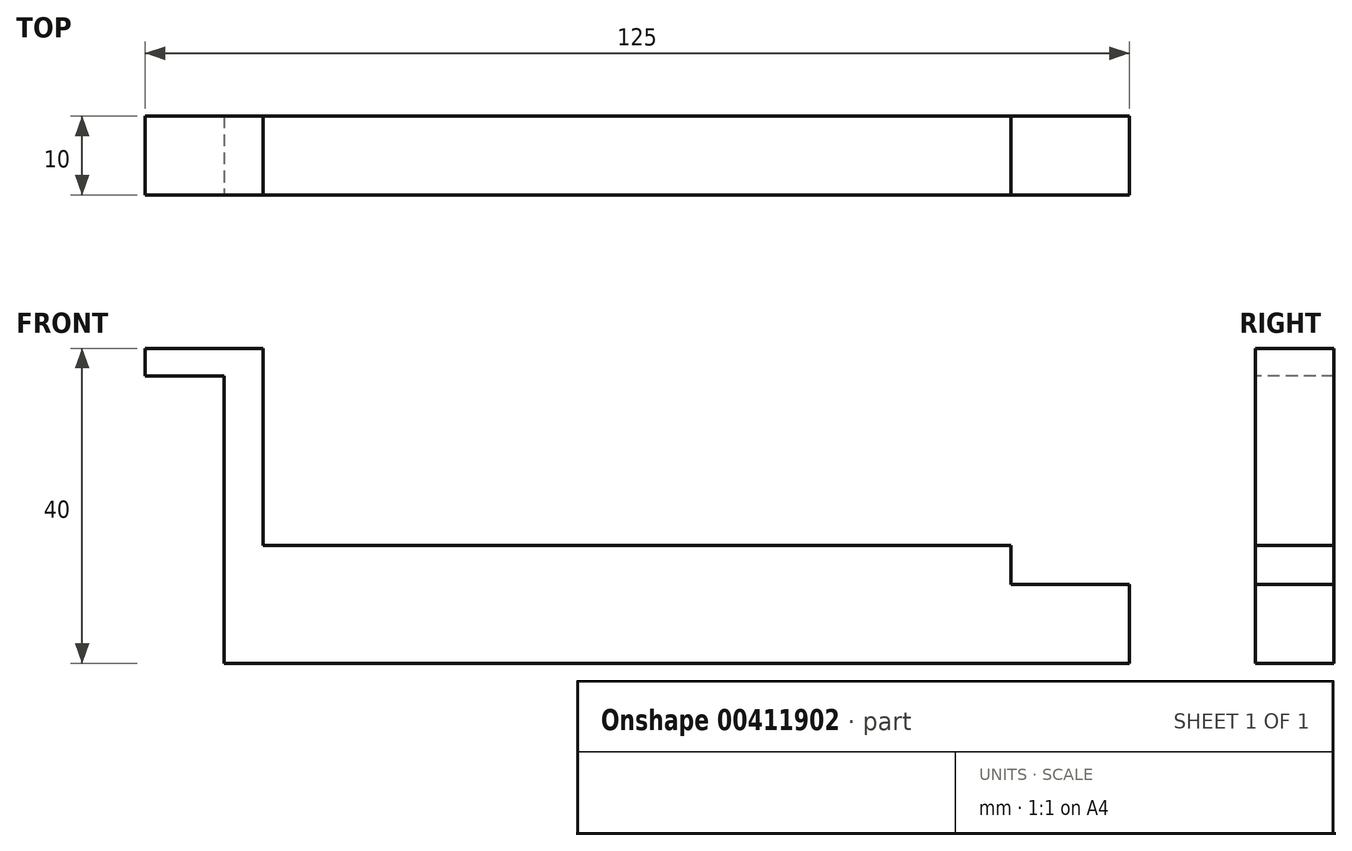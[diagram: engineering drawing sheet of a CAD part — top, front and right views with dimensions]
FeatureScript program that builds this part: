
annotation { "Feature Type Name" : "Feature", "Feature Type Description" : "" }
export const myFeature = defineFeature(function(context is Context, id is Id, definition is map)
    precondition{}
    {
        {
            var Q0;
            Q0=qCreatedBy(makeId("Front.planeOp"),FACE);
            var sketch = newSketch(context, id + "F0", { "sketchPlane" : qUnion([Q0])});
            skLineSegment(sketch, "E0.bottom", {"start": v(-57.5, 7.5) * mm, "end": v(57.5, 7.5) * mm});
            skLineSegment(sketch, "E0.top", {"start": v(-57.5, -7.5) * mm, "end": v(57.5, -7.5) * mm});
            skLineSegment(sketch, "E0.left", {"start": v(-57.5, 7.5) * mm, "end": v(-57.5, -7.5) * mm});
            skLineSegment(sketch, "E0.right", {"start": v(57.5, 7.5) * mm, "end": v(57.5, -7.5) * mm});
            skSolve(sketch);
        }
        {
            var Q0;
            Q0 = qSketchRegion(id + "F0", true);
            extrude(context, id + "F1", {"entities" : qUnion([Q0]), "depth" : 10 * mm});
        }
        {
            var Q0;
            Q0=makeQuery(id+"F1.opExtrude","SWEPT_FACE",FACE,{"disambiguationData":[OSD([sQuery(id+"F0.wireOp",EDGE,"E0.bottom")])]});
            var sketch = newSketch(context, id + "F2", { "sketchPlane" : qUnion([Q0])});
            skLineSegment(sketch, "E1.bottom", {"start": v(57.5, 0) * mm, "end": v(42.5, 0) * mm});
            skLineSegment(sketch, "E1.top", {"start": v(57.5, -10) * mm, "end": v(42.5, -10) * mm});
            skLineSegment(sketch, "E1.left", {"start": v(57.5, 0) * mm, "end": v(57.5, -10) * mm});
            skLineSegment(sketch, "E1.right", {"start": v(42.5, 0) * mm, "end": v(42.5, -10) * mm});
            skSolve(sketch);
        }
        {
            var Q0;
            Q0=makeQuery(id+"F2.imprint","IMPRINT",FACE,{"disambiguationData":[TD([[makeQuery(id+"F2.imprint","IMPRINT",EDGE,{"derivedFrom":sQuery(id+"F2.wireOp",EDGE,"E1.bottom")}),-1.0]])]});
            extrude(context, id + "F3", {"entities" : qUnion([Q0]), "operationType" : NewBodyOperationType.REMOVE, "oppositeDirection" : true, "depth" : 5 * mm});
        }
        {
            var Q0;
            Q0=makeQuery(id+"F1.opExtrude","SWEPT_FACE",FACE,{"disambiguationData":[OSD([sQuery(id+"F0.wireOp",EDGE,"E0.bottom")])]});
            var sketch = newSketch(context, id + "F4", { "sketchPlane" : qUnion([Q0])});
            skLineSegment(sketch, "E2.bottom", {"start": v(-52.5, 0) * mm, "end": v(-57.5, 0) * mm});
            skLineSegment(sketch, "E2.top", {"start": v(-52.5, -10) * mm, "end": v(-57.5, -10) * mm});
            skLineSegment(sketch, "E2.left", {"start": v(-52.5, 0) * mm, "end": v(-52.5, -10) * mm});
            skLineSegment(sketch, "E2.right", {"start": v(-57.5, 0) * mm, "end": v(-57.5, -10) * mm});
            skSolve(sketch);
        }
        {
            var Q0;
            Q0=makeQuery(id+"F4.imprint","IMPRINT",FACE,{"disambiguationData":[TD([[makeQuery(id+"F4.imprint","IMPRINT",EDGE,{"derivedFrom":sQuery(id+"F4.wireOp",EDGE,"E2.bottom")}),-1.0]])]});
            extrude(context, id + "F5", {"entities" : qUnion([Q0]), "operationType" : NewBodyOperationType.ADD, "depth" : 25 * mm});
        }
        {
            var Q0;
            Q0=makeQuery(id+"F5.boolean.opBoolean","MERGE",FACE,{"derivedFrom":[makeQuery(id+"F1.opExtrude","SWEPT_FACE",FACE,{"disambiguationData":[OSD([sQuery(id+"F0.wireOp",EDGE,"E0.left")])]}),makeQuery(id+"F5.opExtrude","SWEPT_FACE",FACE,{"disambiguationData":[OSD([sQuery(id+"F4.wireOp",EDGE,"E2.right")])]})]});
            var sketch = newSketch(context, id + "F6", { "sketchPlane" : qUnion([Q0])});
            skLineSegment(sketch, "E3.bottom", {"start": v(0, 32.5) * mm, "end": v(10, 32.5) * mm});
            skLineSegment(sketch, "E3.top", {"start": v(0, 29) * mm, "end": v(10, 29) * mm});
            skLineSegment(sketch, "E3.left", {"start": v(0, 32.5) * mm, "end": v(0, 29) * mm});
            skLineSegment(sketch, "E3.right", {"start": v(10, 32.5) * mm, "end": v(10, 29) * mm});
            skSolve(sketch);
        }
        {
            var Q0;
            Q0=makeQuery(id+"F6.imprint","IMPRINT",FACE,{"disambiguationData":[TD([[makeQuery(id+"F6.imprint","IMPRINT",EDGE,{"derivedFrom":sQuery(id+"F6.wireOp",EDGE,"E3.bottom")}),1.0]])]});
            extrude(context, id + "F7", {"entities" : qUnion([Q0]), "operationType" : NewBodyOperationType.ADD, "depth" : 10 * mm});
        }
    });
